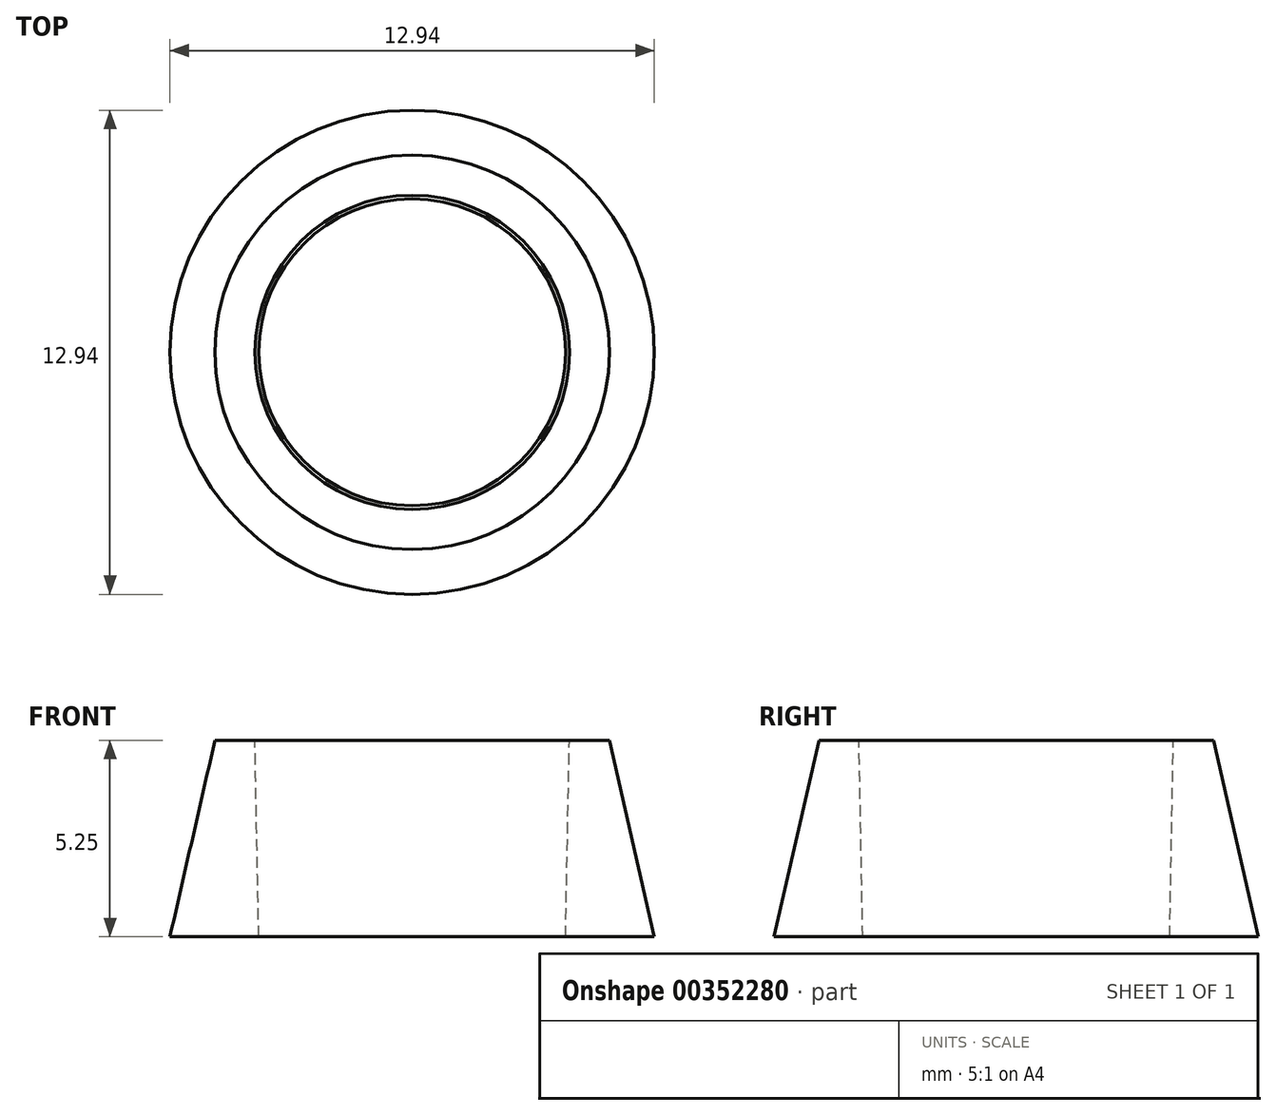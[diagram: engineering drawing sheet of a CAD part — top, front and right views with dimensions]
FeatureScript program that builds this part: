
annotation { "Feature Type Name" : "Feature", "Feature Type Description" : "" }
export const myFeature = defineFeature(function(context is Context, id is Id, definition is map)
    precondition{}
    {
        {
            var Q0;
            Q0=qCreatedBy(makeId("Front.planeOp"),FACE);
            var sketch = newSketch(context, id + "F0", { "sketchPlane" : qUnion([Q0])});
            skLineSegment(sketch, "E0", {"start": v(0, 0) * mm, "end": v(0, 3.15) * mm, "construction": true});
            skLineSegment(sketch, "E1", {"start": v(0, 3.15) * mm, "end": v(0, 8.4) * mm, "construction": true});
            skPoint(sketch, "E2.endSnap0", {"position": v(0, 5.77) * mm});
            skLineSegment(sketch, "E3", {"start": v(4.1, 3.15) * mm, "end": v(6.47, 3.15) * mm});
            skLineSegment(sketch, "E4", {"start": v(5.27, 8.4) * mm, "end": v(6.47, 3.15) * mm});
            skLineSegment(sketch, "E5", {"start": v(4.2, 8.4) * mm, "end": v(5.27, 8.4) * mm});
            skLineSegment(sketch, "E6", {"start": v(0, 3.15) * mm, "end": v(4.1, 3.15) * mm, "construction": true});
            skLineSegment(sketch, "E7", {"start": v(0, 8.4) * mm, "end": v(4.2, 8.4) * mm, "construction": true});
            skLineSegment(sketch, "E8", {"start": v(4.1, 3.15) * mm, "end": v(4.2, 8.4) * mm});
            skSolve(sketch);
        }
        {
            var Q0;
            Q0 = qSketchRegion(id + "F0", true);
            var Q1;
            Q1=sQuery(id+"F0.wireOp",EDGE,"E1");
            revolve(context, id + "F1", {"entities" : qUnion([Q0]), "axis" : qUnion([Q1]), "revolveType" : RevolveType.FULL});
        }
    });
